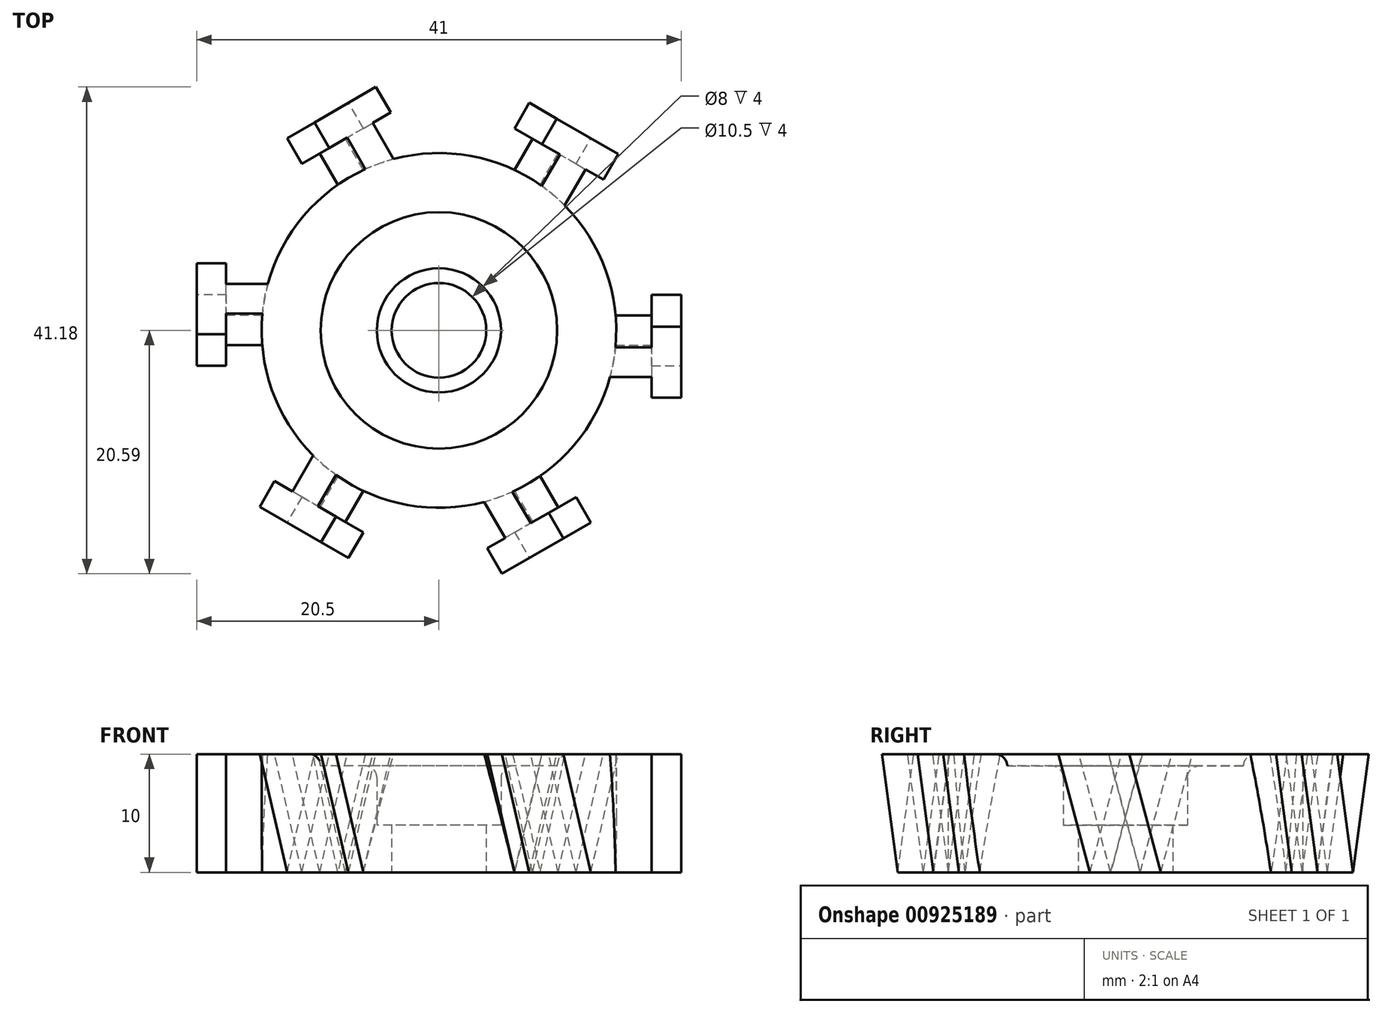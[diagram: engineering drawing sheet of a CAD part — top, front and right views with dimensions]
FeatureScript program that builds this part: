
annotation { "Feature Type Name" : "Feature", "Feature Type Description" : "" }
export const myFeature = defineFeature(function(context is Context, id is Id, definition is map)
    precondition{}
    {
        {
            var Q0;
            Q0=qCreatedBy(makeId("Top.planeOp"),FACE);
            var sketch = newSketch(context, id + "F0", { "sketchPlane" : qUnion([Q0])});
            skCircle(sketch, "E0", {"center": v(0, 0) * mm, "radius": 5.25 * mm});
            skCircle(sketch, "E1", {"center": v(0, 0) * mm, "radius": 10 * mm});
            skCircle(sketch, "E2", {"center": v(0, 0) * mm, "radius": 15 * mm});
            skCircle(sketch, "E3", {"center": v(0, 0) * mm, "radius": 4 * mm});
            skSolve(sketch);
        }
        {
            var Q0;
            Q0=qCreatedBy(makeId("Top.planeOp"),FACE);
            var sketch = newSketch(context, id + "F1", { "sketchPlane" : qUnion([Q0])});
            skLineSegment(sketch, "E4.bottom", {"start": v(-12, 1.25) * mm, "end": v(-18, 1.25) * mm});
            skLineSegment(sketch, "E4.top", {"start": v(-12, -1.25) * mm, "end": v(-18, -1.25) * mm});
            skLineSegment(sketch, "E4.left", {"start": v(-12, 1.25) * mm, "end": v(-12, -1.25) * mm});
            skLineSegment(sketch, "E4.right", {"start": v(-18, 1.25) * mm, "end": v(-18, -1.25) * mm});
            skPoint(sketch, "E4.middle", {"position": v(-15, 0) * mm});
            skLineSegment(sketch, "E5.bottom", {"start": v(-18, 3) * mm, "end": v(-20.5, 3) * mm});
            skLineSegment(sketch, "E5.top", {"start": v(-18, -3) * mm, "end": v(-20.5, -3) * mm});
            skLineSegment(sketch, "E5.left", {"start": v(-18, 3) * mm, "end": v(-18, -3) * mm});
            skLineSegment(sketch, "E5.right", {"start": v(-20.5, 3) * mm, "end": v(-20.5, -3) * mm});
            skPoint(sketch, "E5.middle", {"position": v(-19.25, 0) * mm});
            skPoint(sketch, "E5.middle.positionSnap0", {"position": v(-18, 0) * mm});
            skPoint(sketch, "E5.cornerSnap0", {"position": v(-18, 0) * mm});
            skPoint(sketch, "E5.centerSnap0", {"position": v(-18, 0) * mm});
            skSolve(sketch);
        }
        {
            var Q0;
            Q0=makeQuery(id+"F0.imprint","IMPRINT",FACE,{"disambiguationData":[TD([[makeQuery(id+"F0.imprint","IMPRINT",EDGE,{"derivedFrom":sQuery(id+"F0.wireOp",EDGE,"E1")}),-1.0]])]});
            extrude(context, id + "F2", {"entities" : qUnion([Q0]), "depth" : 10 * mm, "offsetDistance" : 25 * mm});
        }
        {
            var Q0;
            Q0=sQuery(id+"F1.wireOp",EDGE,"E4.left");
            cPoint(context, id + "F3", {"entities" : qUnion([Q0]), "parameter" : 0.5});
        }
        {
            var Q0;
            Q0=qCreatedBy(makeId("Right.planeOp"),FACE);
            var Q1;
            Q1 = qCreatedBy(id + "F3" ,VERTEX);
            cPlane(context, id + "F4", {"entities" : qUnion([Q0, Q1]), "cplaneType" : CPlaneType.PLANE_POINT, "offset" : 25 * mm, "width" : 150 * mm, "height" : 150 * mm});
        }
        {
            var Q0;
            Q0=qCreatedBy(id+"F4.planeOp",FACE);
            var sketch = newSketch(context, id + "F5", { "sketchPlane" : qUnion([Q0])});
            skLineSegment(sketch, "E6", {"start": v(-1.25, 0) * mm, "end": v(1.43, 10) * mm});
            skSolve(sketch);
        }
        {
            var Q0;
            {var subQ3=sQuery(id+"F1.wireOp",EDGE,"E5.bottom");Q0=makeQuery(id+"F1.imprint","IMPRINT",FACE,{"disambiguationData":[TD([[makeQuery(id+"F1.imprint","IMPRINT",EDGE,{"derivedFrom":subQ3}),1.0]])]});}
            var Q1;
            {var subQ0=sQuery(id+"F1.wireOp",EDGE,"E4.bottom");Q1=makeQuery(id+"F1.imprint","IMPRINT",FACE,{"disambiguationData":[TD([[makeQuery(id+"F1.imprint","IMPRINT",EDGE,{"derivedFrom":subQ0}),1.0]])]});}
            var Q2;
            Q2=sQuery(id+"F5.wireOp",EDGE,"E6");
            sweep(context, id + "F6", {"operationType" : NewBodyOperationType.ADD, "profiles" : qUnion([Q0, Q1]), "path" : qUnion([Q2])});
        }
        {
            var Q0;
            Q0=makeQuery(id+"F2.opExtrude","SWEPT_BODY",BODY,{"disambiguationData":[OSD([sQuery(id+"F0.wireOp",EDGE,"E1"),sQuery(id+"F0.wireOp",EDGE,"E2")])]});
            var Q1;
            Q1=sQuery(id+"F0.wireOp",EDGE,"E3");
            circularPattern(context, id + "F7", {"operationType" : NewBodyOperationType.ADD, "entities" : qUnion([Q0]), "axis" : qUnion([Q1]), "angle" : 360 * degree, "instanceCount" : 6, "equalSpace" : true});
        }
        {
            var Q0;
            Q0=qCreatedBy(makeId("Top.planeOp"),FACE);
            var sketch = newSketch(context, id + "F8", { "sketchPlane" : qUnion([Q0])});
            skSolve(sketch);
        }
        {
            var Q0;
            Q0 = qSketchRegion(id + "F8", true);
            var Q1;
            Q1=makeQuery(id+"F0.imprint","IMPRINT",FACE,{"disambiguationData":[TD([[makeQuery(id+"F0.imprint","IMPRINT",EDGE,{"derivedFrom":sQuery(id+"F0.wireOp",EDGE,"E0")}),1.0]])]});
            extrude(context, id + "F9", {"entities" : qUnion([Q0, Q1]), "depth" : 4 * mm, "offsetDistance" : 25 * mm});
        }
        {
            var Q0;
            Q0=makeQuery(id+"F0.imprint","IMPRINT",FACE,{"disambiguationData":[TD([[makeQuery(id+"F0.imprint","IMPRINT",EDGE,{"derivedFrom":sQuery(id+"F0.wireOp",EDGE,"E0")}),-1.0]])]});
            extrude(context, id + "F10", {"entities" : qUnion([Q0]), "operationType" : NewBodyOperationType.ADD, "depth" : 9 * mm, "offsetDistance" : 25 * mm});
        }
        {
            var Q0;
            Q0=makeQuery(id+"F2.opExtrude","CAP_EDGE",EDGE,{"disambiguationData":[OSD([sQuery(id+"F0.wireOp",EDGE,"E1")])],"isStart":false});
            var Q1;
            Q1=makeQuery(id+"F10.opExtrude","CAP_EDGE",EDGE,{"disambiguationData":[OSD([sQuery(id+"F0.wireOp",EDGE,"E0")])],"isStart":false});
            fillet(context, id + "F11", {"entities" : qUnion([Q0, Q1]), "radius" : 1 * mm, "tangentPropagation" : true, "allowEdgeOverflow" : false});
        }
    });
